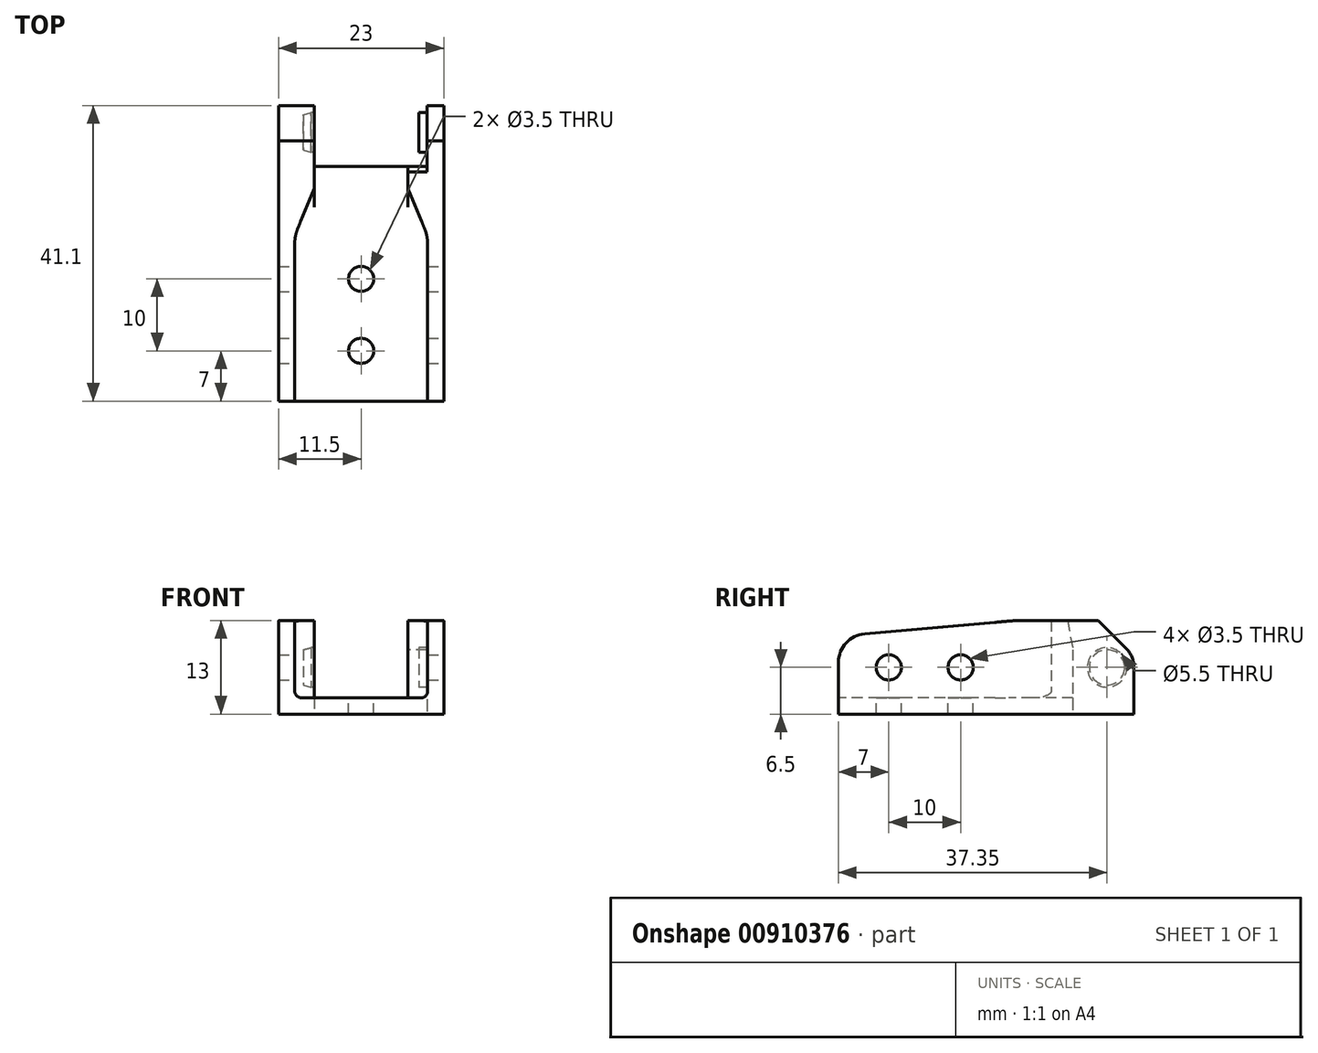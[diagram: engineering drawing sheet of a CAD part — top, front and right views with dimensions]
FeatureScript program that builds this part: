
annotation { "Feature Type Name" : "Feature", "Feature Type Description" : "" }
export const myFeature = defineFeature(function(context is Context, id is Id, definition is map)
    precondition{}
    {
        {
            var Q0;
            Q0=qCreatedBy(makeId("Top.planeOp"),FACE);
            var sketch = newSketch(context, id + "F0", { "sketchPlane" : qUnion([Q0])});
            skLineSegment(sketch, "E0", {"start": v(0, 0) * mm, "end": v(0, 30) * mm, "construction": true});
            skLineSegment(sketch, "E1", {"start": v(0, 30) * mm, "end": v(6.5, 30) * mm});
            skLineSegment(sketch, "E2", {"start": v(6.5, 30) * mm, "end": v(6.5, 38.5) * mm});
            skLineSegment(sketch, "E3", {"start": v(6.5, 38.5) * mm, "end": v(11.5, 38.5) * mm});
            skLineSegment(sketch, "E4", {"start": v(11.5, 38.5) * mm, "end": v(11.5, -2.6) * mm});
            skLineSegment(sketch, "E5", {"start": v(11.5, -2.6) * mm, "end": v(6.5, -2.6) * mm});
            skLineSegment(sketch, "E6", {"start": v(6.5, -2.6) * mm, "end": v(6.5, 0) * mm});
            skLineSegment(sketch, "E7", {"start": v(6.5, 0) * mm, "end": v(0, 0) * mm});
            skLineSegment(sketch, "E8.MirrorCS", {"start": v(0, 30) * mm, "end": v(-6.5, 30) * mm});
            skLineSegment(sketch, "E9.MirrorCS", {"start": v(-6.5, 30) * mm, "end": v(-6.5, 38.5) * mm});
            skLineSegment(sketch, "E10.MirrorCS", {"start": v(-6.5, 0) * mm, "end": v(0, 0) * mm});
            skLineSegment(sketch, "E11.MirrorCS", {"start": v(-11.5, 38.5) * mm, "end": v(-11.5, -2.6) * mm});
            skLineSegment(sketch, "E12.MirrorCS", {"start": v(-6.5, -2.6) * mm, "end": v(-6.5, 0) * mm});
            skLineSegment(sketch, "E13.MirrorCS", {"start": v(-11.5, -2.6) * mm, "end": v(-6.5, -2.6) * mm});
            skLineSegment(sketch, "E14.MirrorCS", {"start": v(-6.5, 38.5) * mm, "end": v(-11.5, 38.5) * mm});
            skSolve(sketch);
        }
        {
            var Q0;
            Q0=qSketchRegion(id+"F0",true);
            extrude(context, id + "F1", {"entities" : qUnion([Q0]), "depth" : 13 * mm, "offsetDistance" : 25.4 * mm});
        }
        {
            var Q0;
            Q0=qCreatedBy(makeId("Front.planeOp"),FACE);
            var sketch = newSketch(context, id + "F2", { "sketchPlane" : qUnion([Q0])});
            skLineSegment(sketch, "E15.bottom", {"start": v(-6.5, 13) * mm, "end": v(6.5, 13) * mm});
            skLineSegment(sketch, "E15.top", {"start": v(-6.5, 2.25) * mm, "end": v(6.5, 2.25) * mm});
            skLineSegment(sketch, "E15.left", {"start": v(-6.5, 13) * mm, "end": v(-6.5, 2.25) * mm});
            skLineSegment(sketch, "E15.right", {"start": v(6.5, 13) * mm, "end": v(6.5, 2.25) * mm});
            skPoint(sketch, "E16.visualSharp", {"position": v(6.5, 2.25) * mm});
            skPoint(sketch, "E17.visualSharp", {"position": v(-6.5, 2.25) * mm});
            skSolve(sketch);
        }
        {
            var Q0;
            Q0=qSketchRegion(id+"F2",true);
            extrude(context, id + "F3", {"entities" : qUnion([Q0]), "operationType" : NewBodyOperationType.REMOVE, "endBound" : BoundingType.THROUGH_ALL, "oppositeDirection" : true, "depth" : 25.4 * mm, "offsetDistance" : 25.4 * mm});
        }
        {
            var Q0;
            Q0=qCreatedBy(makeId("Right.planeOp"),FACE);
            var sketch = newSketch(context, id + "F4", { "sketchPlane" : qUnion([Q0])});
            skLineSegment(sketch, "E18", {"start": v(38.5, 13) * mm, "end": v(33.55, 13) * mm});
            skLineSegment(sketch, "E19", {"start": v(33.55, 13) * mm, "end": v(37.4, 9.15) * mm});
            skLineSegment(sketch, "E20", {"start": v(38.5, 13) * mm, "end": v(38.5, 6.5) * mm});
            skArc(sketch, "E21", {"start": v(37.4, 9.15) * mm, "mid": v(38.21, 7.94) * mm, "end": v(38.5, 6.5) * mm});
            skCircle(sketch, "E22", {"center": v(34.75, 6.5) * mm, "radius": 2.88 * mm, "construction": true});
            skCircle(sketch, "E23", {"center": v(4.4, 6.5) * mm, "radius": 1.75 * mm});
            skCircle(sketch, "E24", {"center": v(14.4, 6.5) * mm, "radius": 1.75 * mm});
            skLineSegment(sketch, "E25", {"start": v(22.4, 13) * mm, "end": v(-2.6, 13) * mm});
            skLineSegment(sketch, "E26", {"start": v(-2.6, 13) * mm, "end": v(-2.6, 7.2) * mm});
            skLineSegment(sketch, "E27", {"start": v(21.3, 12.95) * mm, "end": v(1.05, 11.18) * mm});
            skArc(sketch, "E28", {"start": v(22.4, 13) * mm, "mid": v(21.85, 12.99) * mm, "end": v(21.3, 12.95) * mm});
            skArc(sketch, "E29", {"start": v(1.05, 11.18) * mm, "mid": v(-1.55, 9.9) * mm, "end": v(-2.6, 7.2) * mm});
            skSolve(sketch);
        }
        {
            var Q0;
            Q0=qSketchRegion(id+"F4",true);
            extrude(context, id + "F5", {"entities" : qUnion([Q0]), "operationType" : NewBodyOperationType.REMOVE, "endBound" : BoundingType.THROUGH_ALL, "oppositeDirection" : true, "depth" : 25.4 * mm, "offsetDistance" : 25.4 * mm, "hasSecondDirection" : true, "secondDirectionBound" : BoundingType.THROUGH_ALL, "secondDirectionOppositeDirection" : false, "secondDirectionDepth" : 25.4 * mm});
        }
        {
            var Q0;
            Q0=makeQuery(id+"F3.boolean.opBoolean","MERGE",FACE,{"derivedFrom":[makeQuery(id+"F1.opExtrude","SWEPT_FACE",FACE,{"disambiguationData":[OSD([sQuery(id+"F0.wireOp",EDGE,"E2")])]}),makeQuery(id+"F1.opExtrude","SWEPT_FACE",FACE,{"disambiguationData":[OSD([sQuery(id+"F0.wireOp",EDGE,"E6")])]})],"fromTools":[makeQuery(id+"F3.opExtrude","SWEPT_FACE",FACE,{"disambiguationData":[OSD([sQuery(id+"F2.wireOp",EDGE,"E15.right")])]})]});
            var sketch = newSketch(context, id + "F6", { "sketchPlane" : qUnion([Q0])});
            skLineSegment(sketch, "E30", {"start": v(-30, 0) * mm, "end": v(-30, 8.96) * mm});
            skLineSegment(sketch, "E31.0", {"start": v(-37.4, 9.15) * mm, "end": v(-33.55, 13) * mm});
            skArc(sketch, "E31.1", {"start": v(-38.5, 6.5) * mm, "mid": v(-38.21, 7.94) * mm, "end": v(-37.4, 9.15) * mm});
            skLineSegment(sketch, "E31.2", {"start": v(-38.5, 6.5) * mm, "end": v(-38.5, 0) * mm});
            skLineSegment(sketch, "E32", {"start": v(-38.5, 0) * mm, "end": v(-30, 0) * mm});
            skLineSegment(sketch, "E33", {"start": v(-33.55, 13) * mm, "end": v(-29.29, 13) * mm});
            skCircle(sketch, "E34", {"center": v(-34.75, 6.5) * mm, "radius": 2.75 * mm});
            skLineSegment(sketch, "E35", {"start": v(-29.29, 13) * mm, "end": v(-30, 8.96) * mm});
            skPoint(sketch, "E36", {"position": v(-27.98, 13) * mm});
            skSolve(sketch);
        }
        {
            var Q0;
            Q0=qSketchRegion(id+"F6",true);
            var Q1;
            Q1=makeQuery(id+"F1.opExtrude","SWEPT_FACE",FACE,{"disambiguationData":[OSD([sQuery(id+"F0.wireOp",EDGE,"SeBJiY7k-StK5-ZHof-btOK-HwGBbINHayP1")])]});
            extrude(context, id + "F7", {"entities" : qUnion([Q0]), "operationType" : NewBodyOperationType.REMOVE, "flatOperationType" : FlatOperationType.REMOVE, "oppositeDirection" : true, "depth" : 2.65 * mm, "endBoundEntityFace" : qUnion([Q1]), "offsetDistance" : .1 * mm, "offsetOppositeDirection" : true, "domain" : OperationDomain.MODEL});
        }
        {
            var Q0;
            Q0=makeQuery(id+"F7.boolean.opBoolean","SPLIT",FACE,{"disambiguationData":[TD([makeQuery(id+"F7.opExtrude","SWEPT_FACE",FACE,{"disambiguationData":[OSD([sQuery(id+"F6.wireOp",EDGE,"E34")])]})])],"derivedFrom":makeQuery(id+"F3.boolean.opBoolean","MERGE",FACE,{"derivedFrom":[makeQuery(id+"F1.opExtrude","SWEPT_FACE",FACE,{"disambiguationData":[OSD([sQuery(id+"F0.wireOp",EDGE,"E2")])]}),makeQuery(id+"F1.opExtrude","SWEPT_FACE",FACE,{"disambiguationData":[OSD([sQuery(id+"F0.wireOp",EDGE,"E6")])]})],"fromTools":[makeQuery(id+"F3.opExtrude","SWEPT_FACE",FACE,{"disambiguationData":[OSD([sQuery(id+"F2.wireOp",EDGE,"E15.right")])]})]})});
            var Q1;
            Q1=makeQuery(id+"FIUSCAmamwmsZPA_1.boolean.opBoolean","COPY",FACE,{"derivedFrom":makeQuery(id+"FIUSCAmamwmsZPA_1.opExtrude","CAP_FACE",FACE,{"disambiguationData":[OSD([sQuery(id+"FArfeVmUC00MCva_1.wireOp",EDGE,"fzvoRFOP-YJKs-XIFh-RY7C-SzvE8x33ROh0")])],"isStart":false})});
            var Q2;
            Q2=makeQuery(id+"F3.boolean.opBoolean","MERGE",FACE,{"derivedFrom":[makeQuery(id+"F1.opExtrude","SWEPT_FACE",FACE,{"disambiguationData":[OSD([sQuery(id+"F0.wireOp",EDGE,"E9.MirrorCS")])]}),makeQuery(id+"F1.opExtrude","SWEPT_FACE",FACE,{"disambiguationData":[OSD([sQuery(id+"F0.wireOp",EDGE,"E12.MirrorCS")])]})],"fromTools":[makeQuery(id+"F3.opExtrude","SWEPT_FACE",FACE,{"disambiguationData":[OSD([sQuery(id+"F2.wireOp",EDGE,"E15.left")])]})]});
            extrude(context, id + "F8", {"entities" : qUnion([Q0]), "operationType" : NewBodyOperationType.REMOVE, "flatOperationType" : FlatOperationType.REMOVE, "oppositeDirection" : true, "depth" : 1.55 * mm, "endBoundEntityFace" : qUnion([Q1]), "offsetDistance" : .25 * mm, "offsetOppositeDirection" : true, "hasSecondDirection" : true, "secondDirectionBound" : BoundingType.UP_TO_SURFACE, "secondDirectionOppositeDirection" : false, "secondDirectionDepth" : 25.4 * mm, "secondDirectionBoundEntityFace" : qUnion([Q2]), "hasSecondDirectionOffset" : true, "secondDirectionOffsetDistance" : 1.55 * mm, "secondDirectionOffsetOppositeDirection" : true, "domain" : OperationDomain.MODEL});
        }
        {
            var Q0;
            Q0=makeQuery(id+"F8.boolean.opBoolean","COPY",EDGE,{"derivedFrom":makeQuery(id+"F8.opExtrude","CAP_EDGE",EDGE,{"disambiguationData":[OSD([sQuery(id+"F6.wireOp",EDGE,"E34")])],"isStart":false})});
            var Q1;
            Q1=makeQuery(id+"F8.boolean.opBoolean","COPY",EDGE,{"derivedFrom":makeQuery(id+"F8.opExtrude","CAP_EDGE",EDGE,{"disambiguationData":[OSD([sQuery(id+"F6.wireOp",EDGE,"E34")])],"isStart":true})});
            chamfer(context, id + "F9", {"entities" : qUnion([Q0, Q1]), "chamferType" : ChamferType.OFFSET_ANGLE, "width" : 1.1 * mm, "oppositeDirection" : true, "angle" : 15 * degree, "tangentPropagation" : true});
        }
        {
            var Q0;
            Q0=makeQuery(id+"F1.opExtrude","SWEPT_FACE",FACE,{"disambiguationData":[OSD([sQuery(id+"F0.wireOp",EDGE,"E7"),sQuery(id+"F0.wireOp",EDGE,"E10.MirrorCS")])]});
            var Q1;
            Q1=makeQuery(id+"F1.opExtrude","SWEPT_FACE",FACE,{"disambiguationData":[OSD([sQuery(id+"F0.wireOp",EDGE,"E13.MirrorCS")])]});
            extrude(context, id + "F10", {"entities" : qUnion([Q0]), "operationType" : NewBodyOperationType.ADD, "endBound" : BoundingType.UP_TO_SURFACE, "depth" : 25.4 * mm, "endBoundEntityFace" : qUnion([Q1]), "offsetDistance" : 25.4 * mm});
        }
        {
            var Q0;
            {var subQ0=sQuery(id+"F2.wireOp",EDGE,"E15.top");Q0=makeQuery(id+"F10.boolean.opBoolean","MERGE",FACE,{"derivedFrom":[makeQuery(id+"F3.boolean.opBoolean","COPY",FACE,{"derivedFrom":makeQuery(id+"F3.opExtrude","SWEPT_FACE",FACE,{"disambiguationData":[OSD([subQ0])]})}),makeQuery(id+"F10.opExtrude","SWEPT_FACE",FACE,{"disambiguationData":[OSD([subQ0])]})]});}
            var sketch = newSketch(context, id + "F11", { "sketchPlane" : qUnion([Q0])});
            skLineSegment(sketch, "E37", {"start": v(9.25, -2.6) * mm, "end": v(9.25, 20.36) * mm});
            skLineSegment(sketch, "E38", {"start": v(9.25, 20.36) * mm, "end": v(6.5, 27) * mm});
            skLineSegment(sketch, "E39", {"start": v(6.5, 27) * mm, "end": v(-6.5, 27) * mm});
            skLineSegment(sketch, "E40", {"start": v(-6.5, 27) * mm, "end": v(-9.25, 20.36) * mm});
            skLineSegment(sketch, "E41", {"start": v(-9.25, 20.36) * mm, "end": v(-9.25, -2.6) * mm});
            skLineSegment(sketch, "E42", {"start": v(-9.25, -2.6) * mm, "end": v(9.25, -2.6) * mm});
            skLineSegment(sketch, "E43", {"start": v(0, 0) * mm, "end": v(0, -2.6) * mm, "construction": true});
            skSolve(sketch);
        }
        {
            var Q0;
            Q0 = qSketchRegion(id + "F11", true);
            extrude(context, id + "F12", {"entities" : qUnion([Q0]), "operationType" : NewBodyOperationType.REMOVE, "endBound" : BoundingType.THROUGH_ALL, "depth" : 25.4 * mm, "offsetDistance" : 25.4 * mm});
        }
        {
            var Q0;
            Q0=makeQuery(id+"F12.boolean.opBoolean","COPY",EDGE,{"derivedFrom":makeQuery(id+"F12.opExtrude","SWEPT_EDGE",EDGE,{"disambiguationData":[OSD([sQuery(id+"F2.wireOp",EDGE,"E15.top"),sQuery(id+"F2.wireOp",EDGE,"E15.right"),sQuery(id+"F11.wireOp",EDGE,"E38"),sQuery(id+"F11.wireOp",EDGE,"E39")])]})});
            var Q1;
            Q1=makeQuery(id+"F12.boolean.opBoolean","COPY",EDGE,{"derivedFrom":makeQuery(id+"F12.opExtrude","SWEPT_EDGE",EDGE,{"disambiguationData":[OSD([sQuery(id+"F11.wireOp",EDGE,"E37"),sQuery(id+"F11.wireOp",EDGE,"E38")])]})});
            var Q2;
            Q2=makeQuery(id+"F12.boolean.opBoolean","COPY",EDGE,{"derivedFrom":makeQuery(id+"F12.opExtrude","SWEPT_EDGE",EDGE,{"disambiguationData":[OSD([sQuery(id+"F2.wireOp",EDGE,"E15.top"),sQuery(id+"F2.wireOp",EDGE,"E15.left"),sQuery(id+"F11.wireOp",EDGE,"E39"),sQuery(id+"F11.wireOp",EDGE,"E40")])]})});
            var Q3;
            Q3=makeQuery(id+"F12.boolean.opBoolean","COPY",EDGE,{"derivedFrom":makeQuery(id+"F12.opExtrude","SWEPT_EDGE",EDGE,{"disambiguationData":[OSD([sQuery(id+"F11.wireOp",EDGE,"E40"),sQuery(id+"F11.wireOp",EDGE,"E41")])]})});
            fillet(context, id + "F13", {"entities" : qUnion([Q0, Q1, Q2, Q3]), "radius" : 6 * mm, "tangentPropagation" : true, "allowEdgeOverflow" : false});
        }
        {
            var Q0;
            Q0=makeQuery(id+"F12.boolean.opBoolean","COPY",EDGE,{"derivedFrom":makeQuery(id+"F12.opExtrude","CAP_EDGE",EDGE,{"disambiguationData":[OSD([sQuery(id+"F11.wireOp",EDGE,"E37")])],"isStart":true})});
            var Q1;
            Q1=makeQuery(id+"F12.boolean.opBoolean","COPY",EDGE,{"derivedFrom":makeQuery(id+"F12.opExtrude","CAP_EDGE",EDGE,{"disambiguationData":[OSD([sQuery(id+"F11.wireOp",EDGE,"E41")])],"isStart":true})});
            fillet(context, id + "F14", {"entities" : qUnion([Q0, Q1]), "radius" : 1 * mm, "tangentPropagation" : true, "allowEdgeOverflow" : false});
        }
        {
            var Q0;
            {var subQ0=sQuery(id+"F2.wireOp",EDGE,"E15.top");Q0=makeQuery(id+"F12.boolean.opBoolean","MERGE",FACE,{"derivedFrom":[makeQuery(id+"F10.boolean.opBoolean","MERGE",FACE,{"derivedFrom":[makeQuery(id+"F3.boolean.opBoolean","COPY",FACE,{"derivedFrom":makeQuery(id+"F3.opExtrude","SWEPT_FACE",FACE,{"disambiguationData":[OSD([subQ0])]})}),makeQuery(id+"F10.opExtrude","SWEPT_FACE",FACE,{"disambiguationData":[OSD([subQ0])]})]})],"fromTools":[makeQuery(id+"F12.opExtrude","CAP_FACE",FACE,{"disambiguationData":[OSD([sQuery(id+"F11.wireOp",EDGE,"E37"),sQuery(id+"F11.wireOp",EDGE,"E38"),sQuery(id+"F11.wireOp",EDGE,"E39"),sQuery(id+"F11.wireOp",EDGE,"E40"),sQuery(id+"F11.wireOp",EDGE,"E41"),sQuery(id+"F11.wireOp",EDGE,"E42")])],"isStart":true})]});}
            var sketch = newSketch(context, id + "F15", { "sketchPlane" : qUnion([Q0])});
            skCircle(sketch, "E44", {"center": v(0, 4.4) * mm, "radius": 1.75 * mm});
            skCircle(sketch, "E45", {"center": v(0, 14.4) * mm, "radius": 1.75 * mm});
            skSolve(sketch);
        }
        {
            var Q0;
            Q0 = qSketchRegion(id + "F15", true);
            extrude(context, id + "F16", {"entities" : qUnion([Q0]), "operationType" : NewBodyOperationType.REMOVE, "endBound" : BoundingType.THROUGH_ALL, "oppositeDirection" : true, "depth" : 25.4 * mm, "offsetDistance" : 25.4 * mm});
        }
    });
